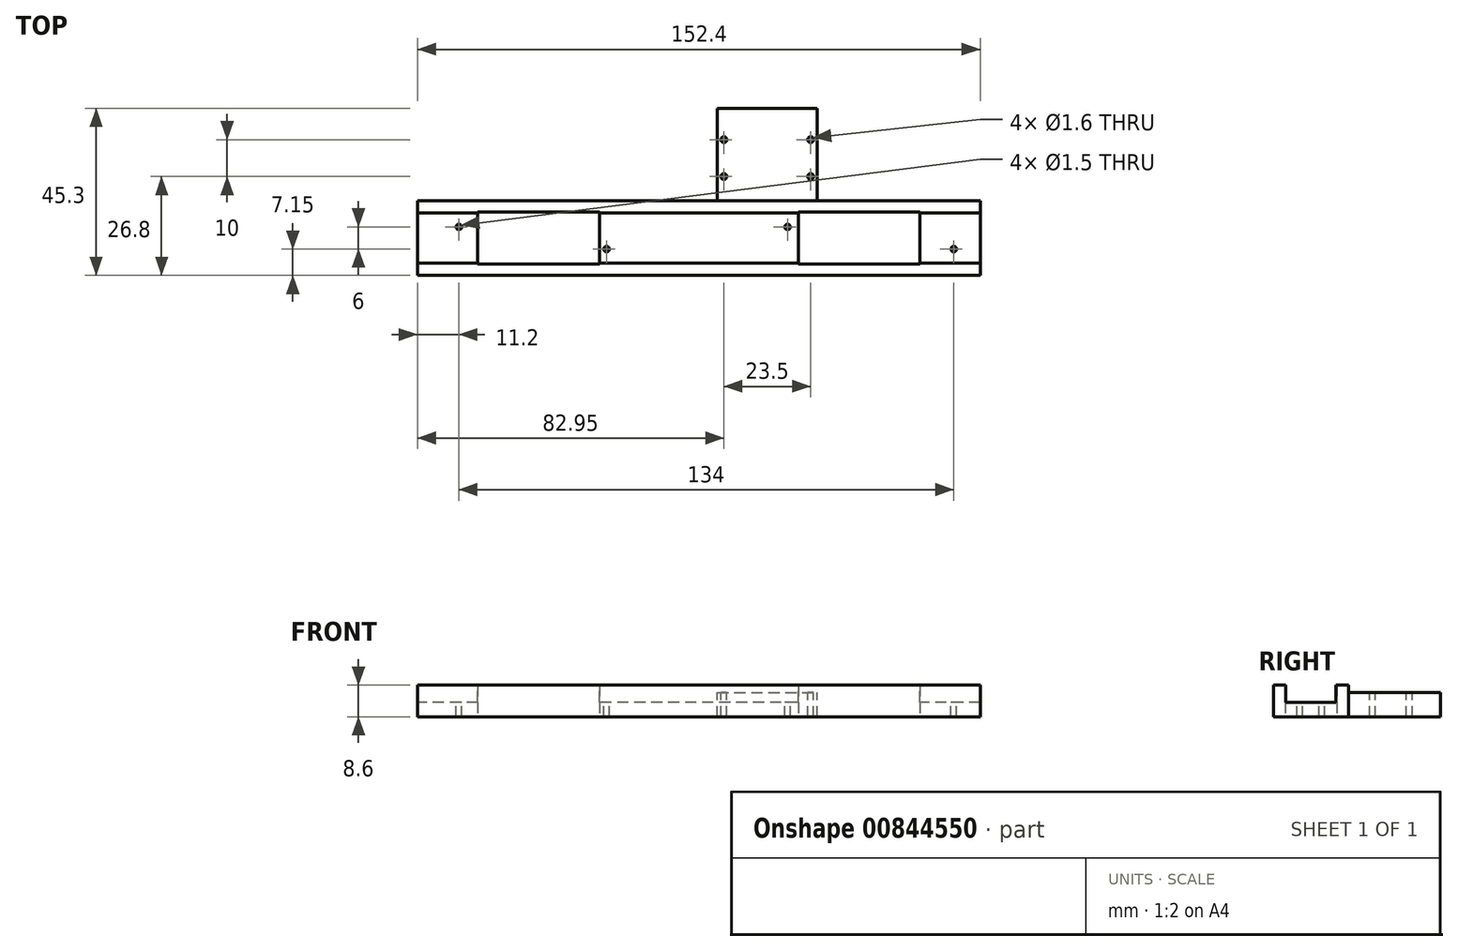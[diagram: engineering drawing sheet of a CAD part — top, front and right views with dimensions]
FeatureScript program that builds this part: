
annotation { "Feature Type Name" : "Feature", "Feature Type Description" : "" }
export const myFeature = defineFeature(function(context is Context, id is Id, definition is map)
    precondition{}
    {
        {
            var Q0;
            Q0=qCreatedBy(makeId("Top.planeOp"),FACE);
            var sketch = newSketch(context, id + "F0", { "sketchPlane" : qUnion([Q0])});
            skLineSegment(sketch, "E0.bottom", {"start": v(76.2, 10.15) * mm, "end": v(-76.2, 10.15) * mm});
            skLineSegment(sketch, "E0.top", {"start": v(76.2, -10.15) * mm, "end": v(-76.2, -10.15) * mm});
            skLineSegment(sketch, "E0.left", {"start": v(76.2, 10.15) * mm, "end": v(76.2, -10.15) * mm});
            skLineSegment(sketch, "E0.right", {"start": v(-76.2, 10.15) * mm, "end": v(-76.2, -10.15) * mm});
            skPoint(sketch, "E0.middle", {"position": v(0, 0) * mm});
            skLineSegment(sketch, "E1.bottom", {"start": v(-26.88, 7) * mm, "end": v(-59.88, 7) * mm});
            skLineSegment(sketch, "E1.top", {"start": v(-26.88, -7) * mm, "end": v(-59.88, -7) * mm});
            skLineSegment(sketch, "E1.left", {"start": v(-26.88, 7) * mm, "end": v(-26.88, -7) * mm});
            skLineSegment(sketch, "E1.right", {"start": v(-59.88, 7) * mm, "end": v(-59.88, -7) * mm});
            skPoint(sketch, "E1.middle", {"position": v(-43.38, 0) * mm});
            skLineSegment(sketch, "E2", {"start": v(0, 0) * mm, "end": v(0, 34.6) * mm, "construction": true});
            skPoint(sketch, "E2.endSnap0", {"position": v(0, 10.15) * mm});
            skLineSegment(sketch, "E3.MirrorCS", {"start": v(26.88, -7) * mm, "end": v(59.88, -7) * mm});
            skLineSegment(sketch, "E4.MirrorCS", {"start": v(26.88, 7) * mm, "end": v(26.88, -7) * mm});
            skPoint(sketch, "E5.MirrorP", {"position": v(43.38, 0) * mm});
            skLineSegment(sketch, "E6.MirrorCS", {"start": v(59.88, 7) * mm, "end": v(59.88, -7) * mm});
            skLineSegment(sketch, "E7.MirrorCS", {"start": v(26.88, 7) * mm, "end": v(59.88, 7) * mm});
            skSolve(sketch);
        }
        {
            var Q0;
            Q0 = qSketchRegion(id + "F0", true);
            extrude(context, id + "F1", {"entities" : qUnion([Q0]), "depth" : 8.6 * mm, "offsetDistance" : 25 * mm});
        }
        {
            var Q0;
            Q0=makeQuery(id+"F1.opExtrude","CAP_FACE",FACE,{"disambiguationData":[OSD([sQuery(id+"F0.wireOp",EDGE,"E0.bottom"),sQuery(id+"F0.wireOp",EDGE,"E0.top"),sQuery(id+"F0.wireOp",EDGE,"E0.left"),sQuery(id+"F0.wireOp",EDGE,"E0.right"),sQuery(id+"F0.wireOp",EDGE,"E1.bottom"),sQuery(id+"F0.wireOp",EDGE,"E1.top"),sQuery(id+"F0.wireOp",EDGE,"E1.left"),sQuery(id+"F0.wireOp",EDGE,"E1.right"),sQuery(id+"F0.wireOp",EDGE,"E3.MirrorCS"),sQuery(id+"F0.wireOp",EDGE,"E4.MirrorCS"),sQuery(id+"F0.wireOp",EDGE,"E6.MirrorCS"),sQuery(id+"F0.wireOp",EDGE,"E7.MirrorCS")])],"isStart":false});
            var sketch = newSketch(context, id + "F2", { "sketchPlane" : qUnion([Q0])});
            skLineSegment(sketch, "E8.bottom", {"start": v(76.2, 6.8) * mm, "end": v(-76.2, 6.8) * mm});
            skLineSegment(sketch, "E8.top", {"start": v(76.2, -6.8) * mm, "end": v(-76.2, -6.8) * mm});
            skLineSegment(sketch, "E8.left", {"start": v(76.2, 6.8) * mm, "end": v(76.2, -6.8) * mm});
            skLineSegment(sketch, "E8.right", {"start": v(-76.2, 6.8) * mm, "end": v(-76.2, -6.8) * mm});
            skPoint(sketch, "E8.middle", {"position": v(0, 0) * mm});
            skSolve(sketch);
        }
        {
            var Q0;
            Q0 = qSketchRegion(id + "F2", true);
            extrude(context, id + "F3", {"entities" : qUnion([Q0]), "operationType" : NewBodyOperationType.REMOVE, "oppositeDirection" : true, "depth" : 4.6 * mm, "offsetDistance" : 25 * mm});
        }
        {
            var Q0;
            {var subQ0=sQuery(id+"F2.wireOp",EDGE,"E8.bottom");var subQ1=sQuery(id+"F2.wireOp",EDGE,"E8.top");Q0=makeQuery(id+"F3.boolean.opBoolean","COPY",FACE,{"disambiguationData":[TD([makeQuery(id+"F1.opExtrude","SWEPT_FACE",FACE,{"disambiguationData":[OSD([sQuery(id+"F0.wireOp",EDGE,"E1.left")])]})])],"derivedFrom":makeQuery(id+"F3.opExtrude","CAP_FACE",FACE,{"disambiguationData":[OSD([subQ0,subQ1,sQuery(id+"F2.wireOp",EDGE,"E8.left"),sQuery(id+"F2.wireOp",EDGE,"E8.right")])],"isStart":false})});}
            var sketch = newSketch(context, id + "F4", { "sketchPlane" : qUnion([Q0])});
            skCircle(sketch, "E9", {"center": v(24, 3) * mm, "radius": 0.75 * mm});
            skCircle(sketch, "E10", {"center": v(-25, -3) * mm, "radius": 0.75 * mm});
            skCircle(sketch, "E11", {"center": v(-65, 3) * mm, "radius": 0.75 * mm});
            skCircle(sketch, "E12", {"center": v(69, -3) * mm, "radius": 0.75 * mm});
            skSolve(sketch);
        }
        {
            var Q0;
            {var subQ0=sQuery(id+"F0.wireOp",EDGE,"E1.bottom");var subQ1=sQuery(id+"F0.wireOp",EDGE,"E0.left");var subQ2=sQuery(id+"F0.wireOp",EDGE,"E0.right");var subQ3=sQuery(id+"F0.wireOp",EDGE,"E0.bottom");var subQ4=sQuery(id+"F0.wireOp",EDGE,"E4.MirrorCS");var subQ5=sQuery(id+"F0.wireOp",EDGE,"E1.left");var subQ6=sQuery(id+"F0.wireOp",EDGE,"E1.right");var subQ7=sQuery(id+"F0.wireOp",EDGE,"E6.MirrorCS");var subQ8=sQuery(id+"F0.wireOp",EDGE,"E7.MirrorCS");Q0=makeQuery(id+"F3.boolean.opBoolean","SPLIT",FACE,{"disambiguationData":[TD([makeQuery(id+"F1.opExtrude","SWEPT_FACE",FACE,{"disambiguationData":[OSD([subQ3])]})])],"derivedFrom":makeQuery(id+"F1.opExtrude","CAP_FACE",FACE,{"disambiguationData":[OSD([subQ3,sQuery(id+"F0.wireOp",EDGE,"E0.top"),subQ1,subQ2,subQ0,sQuery(id+"F0.wireOp",EDGE,"E1.top"),subQ5,subQ6,sQuery(id+"F0.wireOp",EDGE,"E3.MirrorCS"),subQ4,subQ7,subQ8])],"isStart":false})});}
            var sketch = newSketch(context, id + "F5", { "sketchPlane" : qUnion([Q0])});
            skLineSegment(sketch, "E13.bottom", {"start": v(7, 10.15) * mm, "end": v(30, 10.15) * mm});
            skLineSegment(sketch, "E13.top", {"start": v(7, 33.15) * mm, "end": v(30, 33.15) * mm});
            skLineSegment(sketch, "E13.left", {"start": v(7, 10.15) * mm, "end": v(7, 33.15) * mm});
            skLineSegment(sketch, "E13.right", {"start": v(30, 10.15) * mm, "end": v(30, 33.15) * mm});
            skLineSegment(sketch, "E14.bottom", {"start": v(30.25, 26.65) * mm, "end": v(6.75, 26.65) * mm, "construction": true});
            skLineSegment(sketch, "E14.top", {"start": v(30.25, 16.65) * mm, "end": v(6.75, 16.65) * mm, "construction": true});
            skLineSegment(sketch, "E14.left", {"start": v(30.25, 26.65) * mm, "end": v(30.25, 16.65) * mm, "construction": true});
            skLineSegment(sketch, "E14.right", {"start": v(6.75, 26.65) * mm, "end": v(6.75, 16.65) * mm, "construction": true});
            skPoint(sketch, "E14.middle", {"position": v(18.5, 21.65) * mm});
            skPoint(sketch, "E14.middle.positionSnap0", {"position": v(7, 21.65) * mm});
            skPoint(sketch, "E14.middle.positionSnap1", {"position": v(18.5, 33.15) * mm});
            skPoint(sketch, "E14.centerSnap0", {"position": v(7, 21.65) * mm});
            skPoint(sketch, "E14.centerSnap1", {"position": v(18.5, 33.15) * mm});
            skCircle(sketch, "E15", {"center": v(30.25, 26.65) * mm, "radius": 0.8 * mm});
            skCircle(sketch, "E16", {"center": v(30.25, 16.65) * mm, "radius": 0.8 * mm});
            skCircle(sketch, "E17", {"center": v(6.75, 26.65) * mm, "radius": 0.8 * mm});
            skCircle(sketch, "E18", {"center": v(6.75, 16.65) * mm, "radius": 0.8 * mm});
            skLineSegment(sketch, "E19.bottom", {"start": v(32, 35.15) * mm, "end": v(5, 35.15) * mm});
            skLineSegment(sketch, "E19.top", {"start": v(32, 8.15) * mm, "end": v(5, 8.15) * mm});
            skLineSegment(sketch, "E19.left", {"start": v(32, 35.15) * mm, "end": v(32, 8.15) * mm});
            skLineSegment(sketch, "E19.right", {"start": v(5, 35.15) * mm, "end": v(5, 8.15) * mm});
            skSolve(sketch);
        }
        {
            var Q0;
            {var subQ6=sQuery(id+"F5.wireOp",EDGE,"E13.bottom");Q0=makeQuery(id+"F5.imprint","IMPRINT",FACE,{"disambiguationData":[TD([[makeQuery(id+"F5.imprint","IMPRINT",EDGE,{"derivedFrom":subQ6}),-1.0]])]});}
            var Q1;
            {var subQ10=sQuery(id+"F5.wireOp",EDGE,"E13.top");Q1=makeQuery(id+"F5.imprint","IMPRINT",FACE,{"disambiguationData":[TD([[makeQuery(id+"F5.imprint","IMPRINT",EDGE,{"derivedFrom":subQ10}),1.0]])]});}
            var Q2;
            Q2=makeQuery(id+"F1.opExtrude","CAP_FACE",FACE,{"disambiguationData":[OSD([sQuery(id+"F0.wireOp",EDGE,"E0.bottom"),sQuery(id+"F0.wireOp",EDGE,"E0.top"),sQuery(id+"F0.wireOp",EDGE,"E0.left"),sQuery(id+"F0.wireOp",EDGE,"E0.right"),sQuery(id+"F0.wireOp",EDGE,"E1.bottom"),sQuery(id+"F0.wireOp",EDGE,"E1.top"),sQuery(id+"F0.wireOp",EDGE,"E1.left"),sQuery(id+"F0.wireOp",EDGE,"E1.right"),sQuery(id+"F0.wireOp",EDGE,"E3.MirrorCS"),sQuery(id+"F0.wireOp",EDGE,"E4.MirrorCS"),sQuery(id+"F0.wireOp",EDGE,"E6.MirrorCS"),sQuery(id+"F0.wireOp",EDGE,"E7.MirrorCS")])],"isStart":true});
            extrude(context, id + "F6", {"entities" : qUnion([Q0, Q1]), "operationType" : NewBodyOperationType.ADD, "endBound" : BoundingType.UP_TO_SURFACE, "oppositeDirection" : true, "depth" : 4 * mm, "endBoundEntityFace" : qUnion([Q2]), "offsetDistance" : 25 * mm});
        }
        {
            var Q0;
            {var subQ0=sQuery(id+"F0.wireOp",EDGE,"E0.bottom");var subQ1=sQuery(id+"F0.wireOp",EDGE,"E1.bottom");var subQ2=sQuery(id+"F0.wireOp",EDGE,"E0.left");var subQ3=sQuery(id+"F0.wireOp",EDGE,"E0.right");var subQ4=sQuery(id+"F0.wireOp",EDGE,"E4.MirrorCS");var subQ5=sQuery(id+"F0.wireOp",EDGE,"E1.left");var subQ6=sQuery(id+"F0.wireOp",EDGE,"E1.right");var subQ7=sQuery(id+"F0.wireOp",EDGE,"E6.MirrorCS");var subQ8=sQuery(id+"F0.wireOp",EDGE,"E7.MirrorCS");Q0=makeQuery(id+"F6.boolean.opBoolean","MERGE",FACE,{"derivedFrom":[makeQuery(id+"F3.boolean.opBoolean","SPLIT",FACE,{"disambiguationData":[TD([makeQuery(id+"F1.opExtrude","SWEPT_FACE",FACE,{"disambiguationData":[OSD([subQ0])]})])],"derivedFrom":makeQuery(id+"F1.opExtrude","CAP_FACE",FACE,{"disambiguationData":[OSD([subQ0,sQuery(id+"F0.wireOp",EDGE,"E0.top"),subQ2,subQ3,subQ1,sQuery(id+"F0.wireOp",EDGE,"E1.top"),subQ5,subQ6,sQuery(id+"F0.wireOp",EDGE,"E3.MirrorCS"),subQ4,subQ7,subQ8])],"isStart":false})}),makeQuery(id+"F6.opExtrude","CAP_FACE",FACE,{"disambiguationData":[OSD([subQ0,sQuery(id+"F5.wireOp",EDGE,"E13.bottom"),sQuery(id+"F5.wireOp",EDGE,"E15"),sQuery(id+"F5.wireOp",EDGE,"E16"),sQuery(id+"F5.wireOp",EDGE,"E17"),sQuery(id+"F5.wireOp",EDGE,"E18"),sQuery(id+"F5.wireOp",EDGE,"E19.bottom"),sQuery(id+"F5.wireOp",EDGE,"E19.left"),sQuery(id+"F5.wireOp",EDGE,"E19.right")])],"isStart":true})]});}
            var sketch = newSketch(context, id + "F7", { "sketchPlane" : qUnion([Q0])});
            skLineSegment(sketch, "E20.bottom", {"start": v(5, 35.15) * mm, "end": v(32, 35.15) * mm});
            skLineSegment(sketch, "E20.top", {"start": v(5, 10.15) * mm, "end": v(32, 10.15) * mm});
            skLineSegment(sketch, "E20.left", {"start": v(5, 35.15) * mm, "end": v(5, 10.15) * mm});
            skLineSegment(sketch, "E20.right", {"start": v(32, 35.15) * mm, "end": v(32, 10.15) * mm});
            skSolve(sketch);
        }
        {
            var Q0;
            Q0 = qSketchRegion(id + "F7", true);
            extrude(context, id + "F8", {"entities" : qUnion([Q0]), "operationType" : NewBodyOperationType.REMOVE, "oppositeDirection" : true, "depth" : 2 * mm, "offsetDistance" : 25 * mm});
        }
        {
            var Q0;
            Q0 = qSketchRegion(id + "F4", true);
            extrude(context, id + "F9", {"entities" : qUnion([Q0]), "operationType" : NewBodyOperationType.REMOVE, "endBound" : BoundingType.THROUGH_ALL, "oppositeDirection" : true, "depth" : 25 * mm, "offsetDistance" : 25 * mm});
        }
    });
